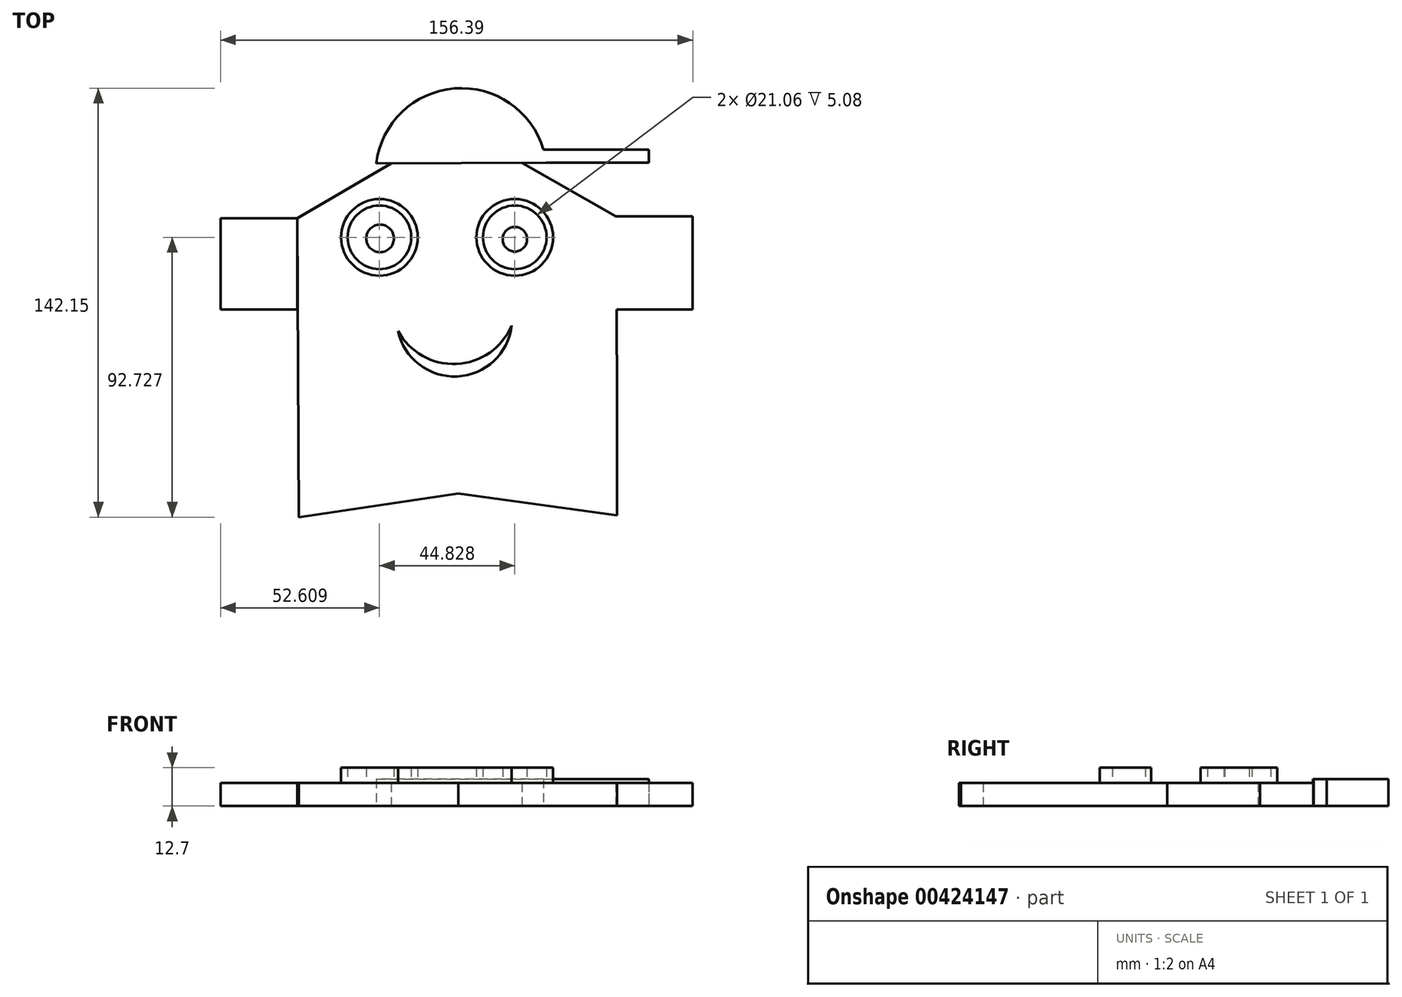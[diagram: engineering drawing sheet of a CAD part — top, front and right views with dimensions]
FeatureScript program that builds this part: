
annotation { "Feature Type Name" : "Feature", "Feature Type Description" : "" }
export const myFeature = defineFeature(function(context is Context, id is Id, definition is map)
    precondition{}
    {
        {
            var Q0;
            Q0=qCreatedBy(makeId("Top.planeOp"),FACE);
            var sketch = newSketch(context, id + "F0", { "sketchPlane" : qUnion([Q0])});
            skCircle(sketch, "E0.cCircle", {"center": v(0, 0) * mm, "radius": 52.8 * mm, "construction": true});
            skLineSegment(sketch, "E0.0", {"start": v(-52.96, 30.2) * mm, "end": v(-0.33, 60.96) * mm});
            skLineSegment(sketch, "E0.1", {"start": v(-0.33, 60.96) * mm, "end": v(52.63, 30.77) * mm});
            skLineSegment(sketch, "E0.2", {"start": v(52.63, 30.77) * mm, "end": v(52.96, -30.2) * mm});
            skLineSegment(sketch, "E0.3", {"start": v(52.96, -30.2) * mm, "end": v(0.33, -60.96) * mm});
            skLineSegment(sketch, "E0.4", {"start": v(0.33, -60.96) * mm, "end": v(-52.63, -30.77) * mm});
            skLineSegment(sketch, "E0.5", {"start": v(-52.63, -30.77) * mm, "end": v(-52.96, 30.2) * mm});
            skPoint(sketch, "E0.0.midPoint", {"position": v(-26.64, 45.58) * mm});
            skLineSegment(sketch, "E1", {"start": v(-52.63, -30.77) * mm, "end": v(-52.42, -68.87) * mm});
            skLineSegment(sketch, "E2", {"start": v(-52.42, -68.87) * mm, "end": v(0.33, -60.96) * mm});
            skLineSegment(sketch, "E3", {"start": v(52.96, -30.2) * mm, "end": v(52.96, -68.3) * mm});
            skLineSegment(sketch, "E4", {"start": v(52.96, -68.3) * mm, "end": v(0.33, -60.96) * mm});
            skLineSegment(sketch, "E5.bottom", {"start": v(-52.96, 30.2) * mm, "end": v(-78.36, 30.2) * mm});
            skLineSegment(sketch, "E5.top", {"start": v(-52.96, 0) * mm, "end": v(-78.36, 0) * mm});
            skLineSegment(sketch, "E5.left", {"start": v(-52.96, 30.2) * mm, "end": v(-52.96, 0) * mm});
            skLineSegment(sketch, "E5.right", {"start": v(-78.36, 30.2) * mm, "end": v(-78.36, 0) * mm});
            skLineSegment(sketch, "E6.bottom", {"start": v(52.63, 30.77) * mm, "end": v(78.03, 30.77) * mm});
            skLineSegment(sketch, "E6.top", {"start": v(52.63, 0) * mm, "end": v(78.03, 0) * mm});
            skLineSegment(sketch, "E6.left", {"start": v(52.63, 30.77) * mm, "end": v(52.63, 0) * mm});
            skLineSegment(sketch, "E6.right", {"start": v(78.03, 30.77) * mm, "end": v(78.03, 0) * mm});
            skSolve(sketch);
        }
        {
            var Q0;
            Q0=makeQuery(id+"F0.imprint","IMPRINT",FACE,{"disambiguationData":[TD([[makeQuery(id+"F0.imprint","IMPRINT",EDGE,{"derivedFrom":sQuery(id+"F0.wireOp",EDGE,"E0.3")}),1.0]])]});
            var Q1;
            {var subQ0=sQuery(id+"F0.wireOp",EDGE,"E6.bottom");Q1=makeQuery(id+"F0.imprint","IMPRINT",FACE,{"disambiguationData":[TD([[makeQuery(id+"F0.imprint","IMPRINT",EDGE,{"derivedFrom":subQ0}),-1.0]])]});}
            var Q2;
            Q2=makeQuery(id+"F0.imprint","IMPRINT",FACE,{"disambiguationData":[TD([[makeQuery(id+"F0.imprint","IMPRINT",EDGE,{"derivedFrom":sQuery(id+"F0.wireOp",EDGE,"E5.bottom")}),1.0]])]});
            var Q3;
            Q3=makeQuery(id+"F0.imprint","IMPRINT",FACE,{"disambiguationData":[TD([[makeQuery(id+"F0.imprint","IMPRINT",EDGE,{"derivedFrom":sQuery(id+"F0.wireOp",EDGE,"E0.4")}),1.0]])]});
            var Q4;
            Q4=makeQuery(id+"F0.imprint","IMPRINT",FACE,{"disambiguationData":[TD([[makeQuery(id+"F0.imprint","IMPRINT",EDGE,{"derivedFrom":sQuery(id+"F0.wireOp",EDGE,"E0.0")}),-1.0]])]});
            var Q5;
            {var subQ0=sQuery(id+"F0.wireOp",EDGE,"E6.left");Q5=makeQuery(id+"F0.imprint","IMPRINT",FACE,{"disambiguationData":[TD([[makeQuery(id+"F0.imprint","IMPRINT",EDGE,{"derivedFrom":subQ0}),1.0]])]});}
            extrude(context, id + "F1", {"entities" : qUnion([Q0, Q1, Q2, Q3, Q4, Q5]), "depth" : 7.62 * mm});
        }
        {
            var Q0;
            Q0=makeQuery(id+"F1.opExtrude","CAP_FACE",FACE,{"disambiguationData":[OSD([sQuery(id+"F0.wireOp",EDGE,"E0.0"),sQuery(id+"F0.wireOp",EDGE,"E0.1"),sQuery(id+"F0.wireOp",EDGE,"E0.2"),sQuery(id+"F0.wireOp",EDGE,"E0.5"),sQuery(id+"F0.wireOp",EDGE,"E1"),sQuery(id+"F0.wireOp",EDGE,"E2"),sQuery(id+"F0.wireOp",EDGE,"E3"),sQuery(id+"F0.wireOp",EDGE,"E4"),sQuery(id+"F0.wireOp",EDGE,"E6.bottom"),sQuery(id+"F0.wireOp",EDGE,"E6.top"),sQuery(id+"F0.wireOp",EDGE,"E6.right")])],"isStart":false});
            var sketch = newSketch(context, id + "F2", { "sketchPlane" : qUnion([Q0])});
            skCircle(sketch, "E7", {"center": v(-25.75, 23.86) * mm, "radius": 10.53 * mm});
            skCircle(sketch, "E8", {"center": v(19.08, 23.86) * mm, "radius": 10.53 * mm});
            skArc(sketch, "E9", {"start": v(-19.6, -7.14) * mm, "mid": v(-0.21, -18.1) * mm, "end": v(18.05, -5.35) * mm});
            skCircle(sketch, "E10", {"center": v(-25.75, 23.86) * mm, "radius": 12.7 * mm});
            skCircle(sketch, "E11", {"center": v(19.08, 23.86) * mm, "radius": 12.7 * mm});
            skArc(sketch, "E12", {"start": v(-19.6, -7.14) * mm, "mid": v(-0.01, -22.23) * mm, "end": v(18.05, -5.35) * mm});
            skSolve(sketch);
        }
        {
            var Q0;
            Q0=makeQuery(id+"F1.opExtrude","CAP_FACE",FACE,{"disambiguationData":[OSD([sQuery(id+"F0.wireOp",EDGE,"E0.0"),sQuery(id+"F0.wireOp",EDGE,"E0.1"),sQuery(id+"F0.wireOp",EDGE,"E0.2"),sQuery(id+"F0.wireOp",EDGE,"E0.5"),sQuery(id+"F0.wireOp",EDGE,"E1"),sQuery(id+"F0.wireOp",EDGE,"E2"),sQuery(id+"F0.wireOp",EDGE,"E3"),sQuery(id+"F0.wireOp",EDGE,"E4"),sQuery(id+"F0.wireOp",EDGE,"E6.bottom"),sQuery(id+"F0.wireOp",EDGE,"E6.top"),sQuery(id+"F0.wireOp",EDGE,"E6.right")])],"isStart":false});
            var sketch = newSketch(context, id + "F3", { "sketchPlane" : qUnion([Q0])});
            skCircle(sketch, "E13", {"center": v(-25.78, 23.46) * mm, "radius": 4.09 * mm});
            skCircle(sketch, "E14", {"center": v(19.1, 23.2) * mm, "radius": 4.06 * mm});
            skSolve(sketch);
        }
        {
            var Q0;
            Q0=makeQuery(id+"F3.imprint","IMPRINT",FACE,{"disambiguationData":[TD([[makeQuery(id+"F3.imprint","IMPRINT",EDGE,{"derivedFrom":sQuery(id+"F3.wireOp",EDGE,"E14")}),1.0]])]});
            extrude(context, id + "F4", {"entities" : qUnion([Q0]), "operationType" : NewBodyOperationType.ADD, "depth" : 5.08 * mm});
        }
        {
            var Q0;
            Q0=makeQuery(id+"F1.opExtrude","CAP_FACE",FACE,{"disambiguationData":[OSD([sQuery(id+"F0.wireOp",EDGE,"E0.0"),sQuery(id+"F0.wireOp",EDGE,"E0.1"),sQuery(id+"F0.wireOp",EDGE,"E0.2"),sQuery(id+"F0.wireOp",EDGE,"E0.5"),sQuery(id+"F0.wireOp",EDGE,"E1"),sQuery(id+"F0.wireOp",EDGE,"E2"),sQuery(id+"F0.wireOp",EDGE,"E3"),sQuery(id+"F0.wireOp",EDGE,"E4"),sQuery(id+"F0.wireOp",EDGE,"E6.bottom"),sQuery(id+"F0.wireOp",EDGE,"E6.top"),sQuery(id+"F0.wireOp",EDGE,"E6.right")])],"isStart":false});
            var sketch = newSketch(context, id + "F5", { "sketchPlane" : qUnion([Q0])});
            skCircle(sketch, "E15", {"center": v(-25.55, 23.5) * mm, "radius": 4.58 * mm});
            skSolve(sketch);
        }
        {
            var Q0;
            Q0=qSketchRegion(id+"F5",true);
            extrude(context, id + "F6", {"entities" : qUnion([Q0]), "operationType" : NewBodyOperationType.ADD, "depth" : 5.08 * mm});
        }
        {
            var Q0;
            Q0=makeQuery(id+"F2.imprint","IMPRINT",FACE,{"disambiguationData":[TD([[makeQuery(id+"F2.imprint","IMPRINT",EDGE,{"derivedFrom":sQuery(id+"F2.wireOp",EDGE,"E7")}),-1.0]])]});
            var Q1;
            Q1=makeQuery(id+"F2.imprint","IMPRINT",FACE,{"disambiguationData":[TD([[makeQuery(id+"F2.imprint","IMPRINT",EDGE,{"derivedFrom":sQuery(id+"F2.wireOp",EDGE,"E8")}),-1.0]])]});
            var Q2;
            Q2=makeQuery(id+"F2.imprint","IMPRINT",FACE,{"disambiguationData":[TD([[makeQuery(id+"F2.imprint","IMPRINT",EDGE,{"derivedFrom":sQuery(id+"F2.wireOp",EDGE,"E9")}),-1.0]])]});
            extrude(context, id + "F7", {"entities" : qUnion([Q0, Q1, Q2]), "operationType" : NewBodyOperationType.ADD, "depth" : 5.08 * mm});
        }
        {
            var Q0;
            Q0=qCreatedBy(makeId("Top.planeOp"),FACE);
            var sketch = newSketch(context, id + "F8", { "sketchPlane" : qUnion([Q0])});
            skArc(sketch, "E16", {"start": v(29.5, 48.52) * mm, "mid": v(1.28, 73.28) * mm, "end": v(-26.8, 48.36) * mm});
            skLineSegment(sketch, "E17.bottom", {"start": v(29.5, 48.52) * mm, "end": v(63.49, 48.52) * mm});
            skLineSegment(sketch, "E17.top", {"start": v(29.5, 52.88) * mm, "end": v(63.49, 52.88) * mm});
            skLineSegment(sketch, "E17.left", {"start": v(29.5, 48.52) * mm, "end": v(29.5, 52.88) * mm});
            skLineSegment(sketch, "E17.right", {"start": v(63.49, 48.52) * mm, "end": v(63.49, 52.88) * mm});
            skLineSegment(sketch, "E18", {"start": v(29.5, 52.88) * mm, "end": v(28.59, 52.88) * mm});
            skLineSegment(sketch, "E19", {"start": v(-26.8, 48.36) * mm, "end": v(29.5, 48.52) * mm});
            skSolve(sketch);
        }
        {
            var Q0;
            Q0=makeQuery(id+"F8.imprint","IMPRINT",FACE,{"disambiguationData":[TD([[makeQuery(id+"F8.imprint","IMPRINT",EDGE,{"derivedFrom":sQuery(id+"F8.wireOp",EDGE,"E17.bottom")}),1.0]])]});
            var Q1;
            {var subQ0=sQuery(id+"F8.wireOp",EDGE,"E17.left");Q1=makeQuery(id+"F8.imprint","IMPRINT",FACE,{"disambiguationData":[TD([[makeQuery(id+"F8.imprint","IMPRINT",EDGE,{"derivedFrom":subQ0}),1.0]])]});}
            var Q2;
            {var subQ0=sQuery(id+"F8.wireOp",EDGE,"E19");Q2=makeQuery(id+"F8.imprint","IMPRINT",FACE,{"disambiguationData":[TD([[makeQuery(id+"F8.imprint","IMPRINT",EDGE,{"derivedFrom":subQ0}),1.0]])]});}
            extrude(context, id + "F9", {"entities" : qUnion([Q0, Q1, Q2]), "operationType" : NewBodyOperationType.ADD, "depth" : 8.9 * mm});
        }
    });
